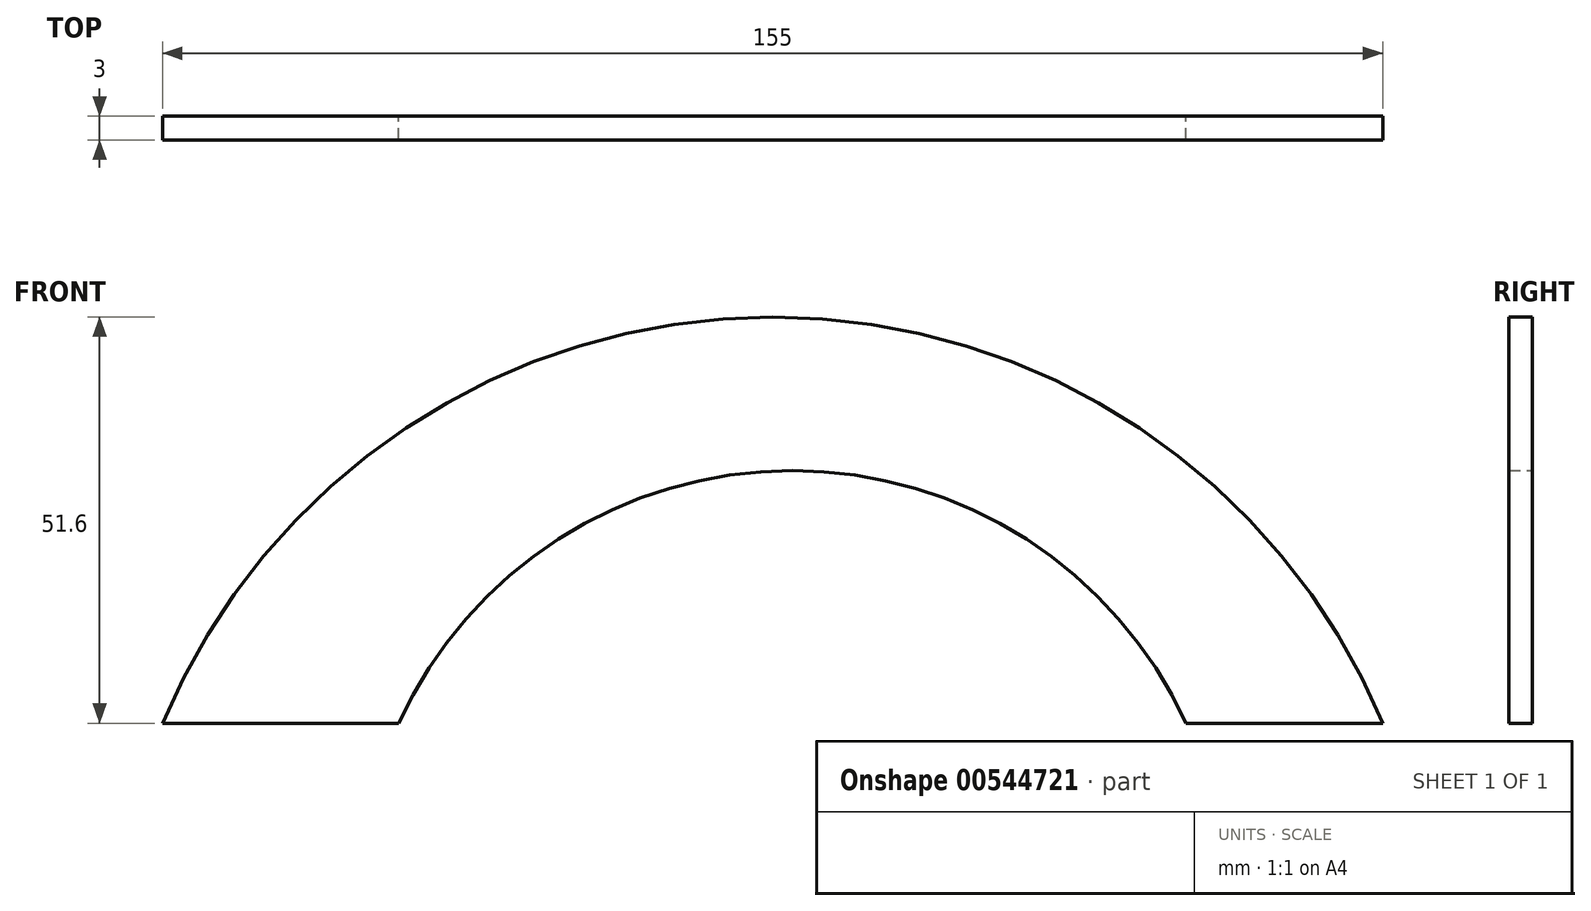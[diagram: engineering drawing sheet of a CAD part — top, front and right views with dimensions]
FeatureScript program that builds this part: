
annotation { "Feature Type Name" : "Feature", "Feature Type Description" : "" }
export const myFeature = defineFeature(function(context is Context, id is Id, definition is map)
    precondition{}
    {
        {
            var Q0;
            Q0=qCreatedBy(makeId("Front.planeOp"),FACE);
            var sketch = newSketch(context, id + "F0", { "sketchPlane" : qUnion([Q0])});
            skLineSegment(sketch, "E0", {"start": v(0, 0) * mm, "end": v(-30, 0) * mm});
            skPoint(sketch, "E1", {"position": v(0, 0) * mm});
            skPoint(sketch, "E2", {"position": v(100, 0) * mm});
            skPoint(sketch, "E3", {"position": v(125, 0) * mm});
            skLineSegment(sketch, "E4", {"start": v(100, 0) * mm, "end": v(125, 0) * mm});
            skArc(sketch, "E5", {"start": v(100, 0) * mm, "mid": v(50, 32.09) * mm, "end": v(0, 0) * mm});
            skArc(sketch, "E6", {"start": v(125, 0) * mm, "mid": v(47.5, 51.6) * mm, "end": v(-30, 0) * mm});
            skSolve(sketch);
        }
        {
            var Q0;
            Q0=qSketchRegion(id+"F0",true);
            extrude(context, id + "F1", {"entities" : qUnion([Q0]), "depth" : 3 * mm});
        }
    });
